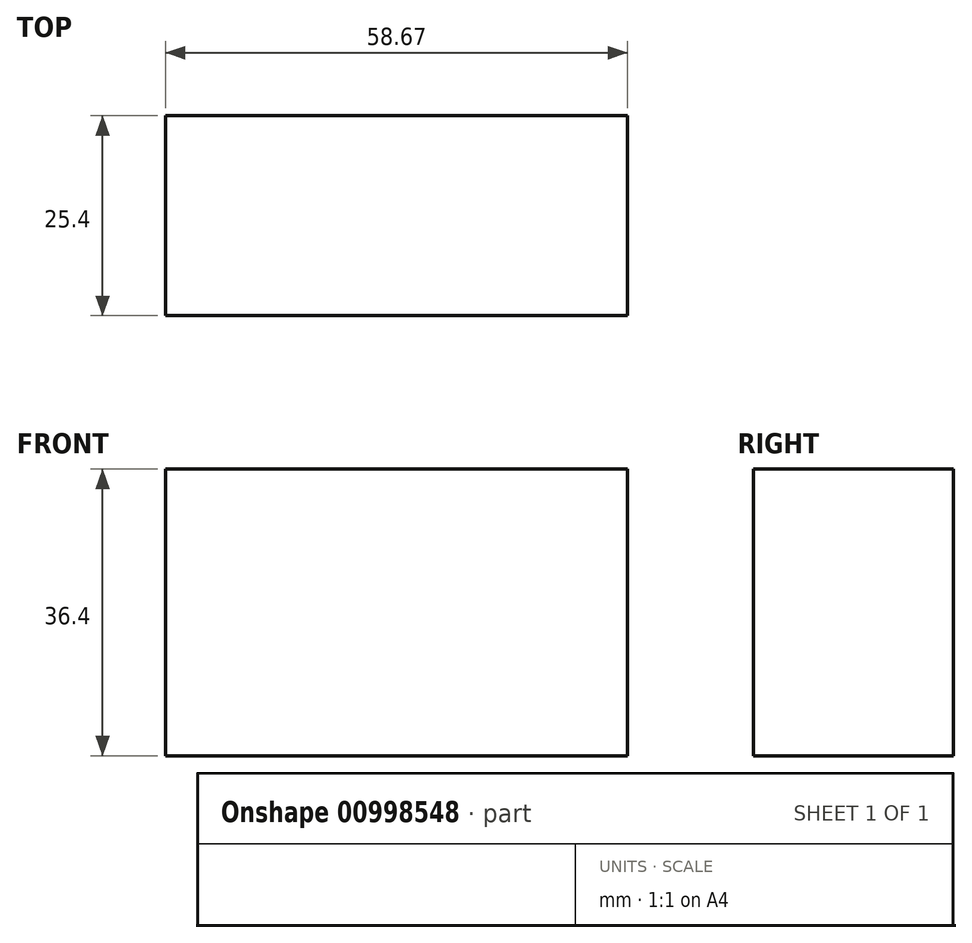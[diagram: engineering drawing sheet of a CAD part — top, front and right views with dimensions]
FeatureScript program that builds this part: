
annotation { "Feature Type Name" : "Feature", "Feature Type Description" : "" }
export const myFeature = defineFeature(function(context is Context, id is Id, definition is map)
    precondition{}
    {
        {
            var Q0;
            Q0=qCreatedBy(makeId("Front.planeOp"),FACE);
            var sketch = newSketch(context, id + "F0", { "sketchPlane" : qUnion([Q0])});
            skLineSegment(sketch, "E0.bottom", {"start": v(-35.4, 20.15) * mm, "end": v(23.26, 20.15) * mm});
            skLineSegment(sketch, "E0.top", {"start": v(-35.4, -16.25) * mm, "end": v(23.26, -16.25) * mm});
            skLineSegment(sketch, "E0.left", {"start": v(-35.4, 20.15) * mm, "end": v(-35.4, -16.25) * mm});
            skLineSegment(sketch, "E0.right", {"start": v(23.26, 20.15) * mm, "end": v(23.26, -16.25) * mm});
            skSolve(sketch);
        }
        {
            var Q0;
            Q0 = qSketchRegion(id + "F0", true);
            extrude(context, id + "F1", {"entities" : qUnion([Q0]), "depth" : 25.4 * mm, "offsetDistance" : 25.4 * mm});
        }
    });
